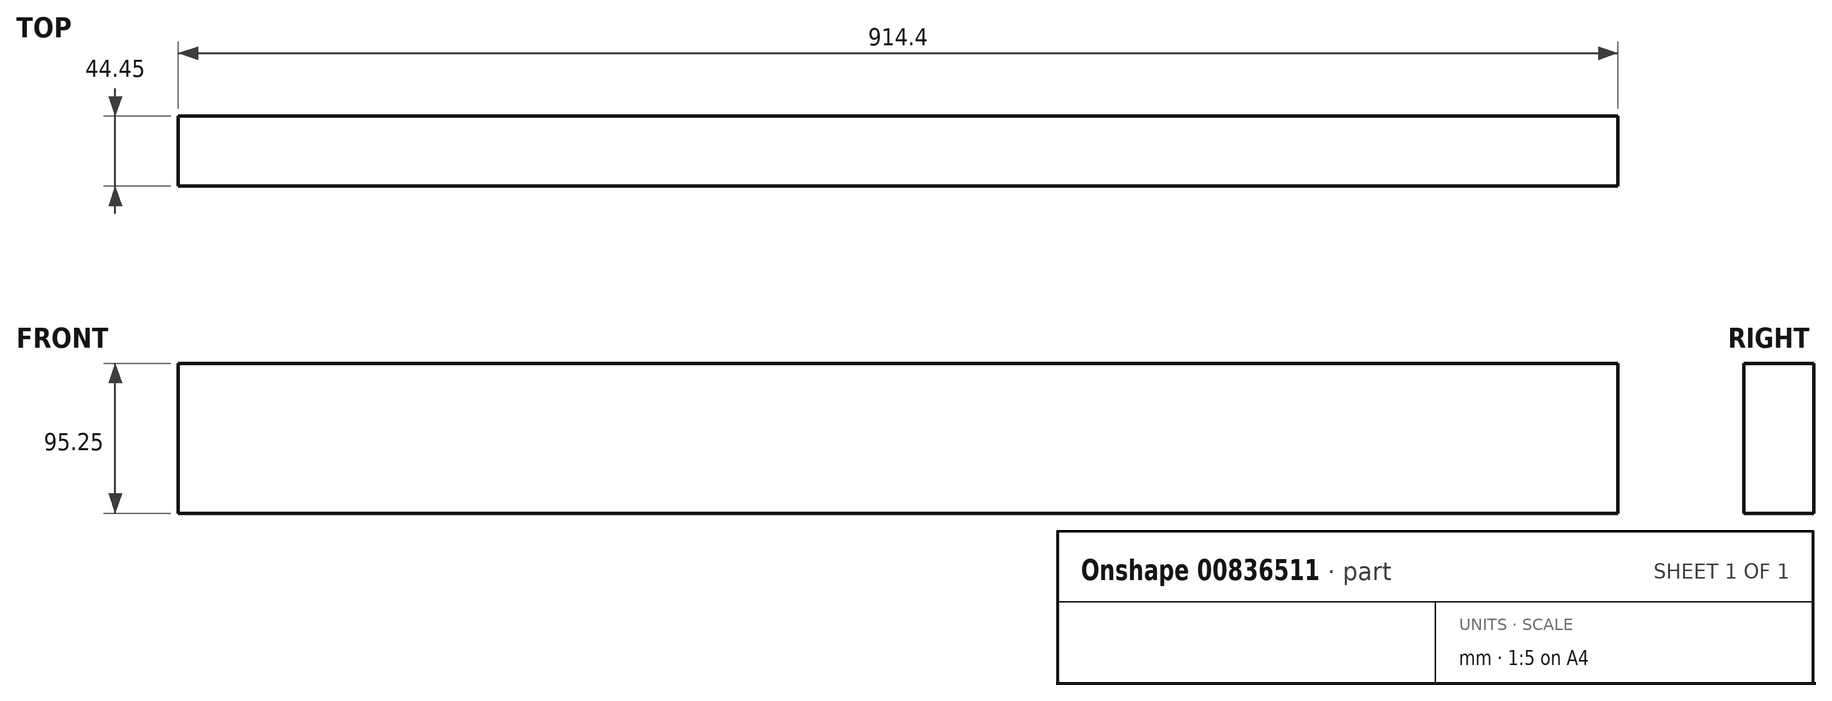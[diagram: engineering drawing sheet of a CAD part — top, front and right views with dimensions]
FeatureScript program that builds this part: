
annotation { "Feature Type Name" : "Feature", "Feature Type Description" : "" }
export const myFeature = defineFeature(function(context is Context, id is Id, definition is map)
    precondition{}
    {
        {
            var Q0;
            Q0=qCreatedBy(makeId("Front.planeOp"),FACE);
            var sketch = newSketch(context, id + "F0", { "sketchPlane" : qUnion([Q0])});
            skLineSegment(sketch, "E0.bottom", {"start": v(0, 0) * mm, "end": v(914.4, 0) * mm});
            skLineSegment(sketch, "E0.top", {"start": v(0, -95.25) * mm, "end": v(914.4, -95.25) * mm});
            skLineSegment(sketch, "E0.left", {"start": v(0, 0) * mm, "end": v(0, -95.25) * mm});
            skLineSegment(sketch, "E0.right", {"start": v(914.4, 0) * mm, "end": v(914.4, -95.25) * mm});
            skSolve(sketch);
        }
        {
            var Q0;
            Q0 = qSketchRegion(id + "F0", true);
            extrude(context, id + "F1", {"entities" : qUnion([Q0]), "depth" : 44.45 * mm, "offsetDistance" : 25.4 * mm});
        }
    });
